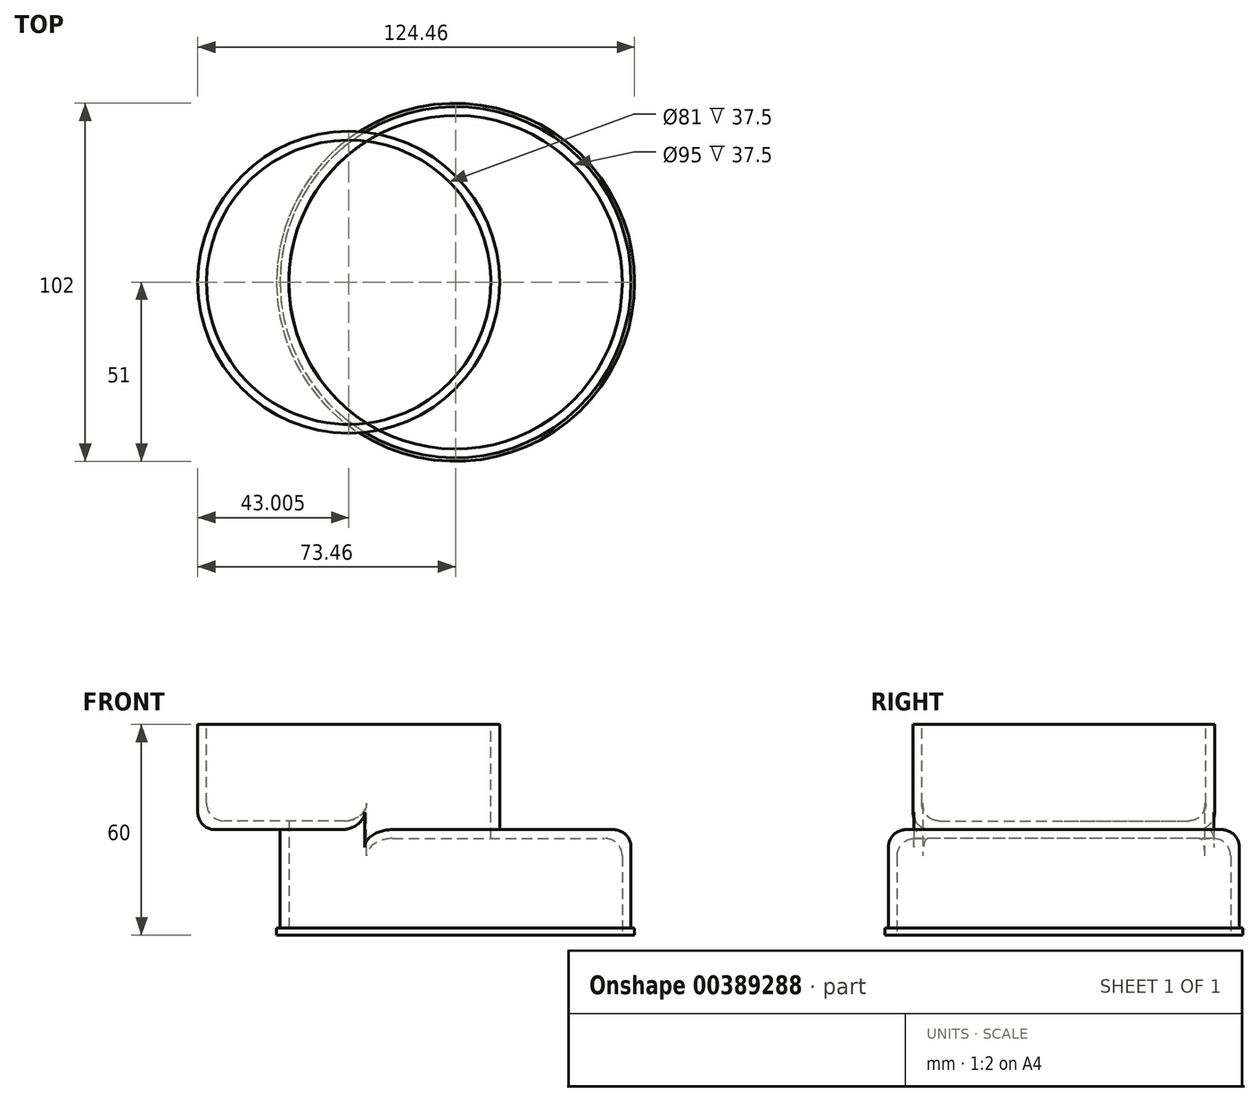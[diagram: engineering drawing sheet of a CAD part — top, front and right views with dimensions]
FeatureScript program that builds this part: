
annotation { "Feature Type Name" : "Feature", "Feature Type Description" : "" }
export const myFeature = defineFeature(function(context is Context, id is Id, definition is map)
    precondition{}
    {
        {
            var Q0;
            Q0=qCreatedBy(makeId("Front.planeOp"),FACE);
            var sketch = newSketch(context, id + "F0", { "sketchPlane" : qUnion([Q0])});
            skLineSegment(sketch, "E0.bottom", {"start": v(0, 0) * mm, "end": v(-50, 0) * mm});
            skLineSegment(sketch, "E0.top", {"start": v(0, 30) * mm, "end": v(-50, 30) * mm});
            skLineSegment(sketch, "E0.left", {"start": v(0, 0) * mm, "end": v(0, 30) * mm});
            skLineSegment(sketch, "E0.right", {"start": v(-50, 0) * mm, "end": v(-50, 30) * mm});
            skLineSegment(sketch, "E1.bottom", {"start": v(-50, 0) * mm, "end": v(-51, 0) * mm});
            skLineSegment(sketch, "E1.top", {"start": v(-50, 2) * mm, "end": v(-51, 2) * mm});
            skLineSegment(sketch, "E1.left", {"start": v(-50, 0) * mm, "end": v(-50, 2) * mm});
            skLineSegment(sketch, "E1.right", {"start": v(-51, 0) * mm, "end": v(-51, 2) * mm});
            skSolve(sketch);
        }
        {
            var Q0;
            Q0=makeQuery(id+"F0.imprint","IMPRINT",FACE,{"disambiguationData":[TD([[makeQuery(id+"F0.imprint","IMPRINT",EDGE,{"derivedFrom":sQuery(id+"F0.wireOp",EDGE,"E0.bottom")}),-1.0]])]});
            var Q1;
            {var subQ0=sQuery(id+"F0.wireOp",EDGE,"E1.bottom");Q1=makeQuery(id+"F0.imprint","IMPRINT",FACE,{"disambiguationData":[TD([[makeQuery(id+"F0.imprint","IMPRINT",EDGE,{"derivedFrom":subQ0}),-1.0]])]});}
            var Q2;
            Q2=sQuery(id+"F0.wireOp",EDGE,"E0.left");
            revolve(context, id + "F1", {"surfaceOperationType" : NewSurfaceOperationType.NEW, "entities" : qUnion([Q0, Q1]), "axis" : qUnion([Q2]), "revolveType" : RevolveType.FULL});
        }
        {
            var Q0;
            Q0=qCreatedBy(makeId("Front.planeOp"),FACE);
            var sketch = newSketch(context, id + "F2", { "sketchPlane" : qUnion([Q0])});
            skLineSegment(sketch, "E2.bottom", {"start": v(-73.46, 60) * mm, "end": v(-30.46, 60) * mm});
            skLineSegment(sketch, "E2.top", {"start": v(-73.46, 30) * mm, "end": v(-30.46, 30) * mm});
            skLineSegment(sketch, "E2.left", {"start": v(-73.46, 60) * mm, "end": v(-73.46, 30) * mm});
            skLineSegment(sketch, "E2.right", {"start": v(-30.46, 60) * mm, "end": v(-30.46, 30) * mm});
            skSolve(sketch);
        }
        {
            var Q0;
            Q0=makeQuery(id+"F2.imprint","IMPRINT",FACE,{"disambiguationData":[TD([[makeQuery(id+"F2.imprint","IMPRINT",EDGE,{"derivedFrom":sQuery(id+"F2.wireOp",EDGE,"E2.bottom")}),-1.0]])]});
            var Q1;
            Q1=qConstructionFilter(qBodyType(qCreatedBy(id+"F2",EDGE),BodyType.WIRE),ConstructionObject.NO);
            var Q2;
            Q2=sQuery(id+"F2.wireOp",EDGE,"E2.right");
            revolve(context, id + "F3", {"surfaceOperationType" : NewSurfaceOperationType.NEW, "entities" : qUnion([Q0]), "surfaceEntities" : qUnion([Q1]), "axis" : qUnion([Q2]), "revolveType" : RevolveType.FULL});
        }
        {
            var Q0;
            Q0=makeQuery(id+"F3.opRevolve","SWEPT_BODY",BODY,{"disambiguationData":[OSD([sQuery(id+"F2.wireOp",EDGE,"E2.bottom"),sQuery(id+"F2.wireOp",EDGE,"E2.top"),sQuery(id+"F2.wireOp",EDGE,"E2.left"),sQuery(id+"F2.wireOp",EDGE,"E2.right")])]});
            var Q1;
            Q1=makeQuery(id+"F1.opRevolve","SWEPT_BODY",BODY,{"disambiguationData":[OSD([sQuery(id+"F0.wireOp",EDGE,"E0.bottom"),sQuery(id+"F0.wireOp",EDGE,"E0.top"),sQuery(id+"F0.wireOp",EDGE,"E0.left"),sQuery(id+"F0.wireOp",EDGE,"E0.right")])]});
            booleanBodies(context, id + "F4", {"operationType" : BooleanOperationType.UNION, "tools" : qUnion([Q0, Q1])});
        }
        {
            var Q0;
            Q0=makeQuery(id+"F1.opRevolve","SWEPT_FACE",FACE,{"disambiguationData":[OSD([sQuery(id+"F0.wireOp",EDGE,"E0.bottom")])]});
            var Q1;
            Q1=makeQuery(id+"F3.opRevolve","SWEPT_FACE",FACE,{"disambiguationData":[OSD([sQuery(id+"F2.wireOp",EDGE,"E2.bottom")])]});
            shell(context, id + "F5", {"entities" : qUnion([Q0, Q1]), "thickness" : 2.5 * mm});
        }
        {
            var Q0;
            {var subQ0=sQuery(id+"F2.wireOp",EDGE,"E2.left");Q0=makeQuery(id+"F4.opBoolean","SPLIT",EDGE,{"disambiguationData":[topologyDisambiguationEdgeConnected([makeQuery(id+"F1.opRevolve","SWEPT_FACE",FACE,{"disambiguationData":[OSD([sQuery(id+"F0.wireOp",EDGE,"E0.top")])]})])],"derivedFrom":makeQuery(id+"F3.opRevolve","SWEPT_EDGE",EDGE,{"disambiguationData":[OSD([sQuery(id+"F2.wireOp",EDGE,"E2.top"),subQ0])]})});}
            fillet(context, id + "F6", {"entities" : qUnion([Q0]), "tangentPropagation" : true, "radius" : 5 * mm, "defaultsChanged" : false, "vertexSettings" : [], "allowEdgeOverflow" : false});
        }
        {
            var Q0;
            {var subQ0=sQuery(id+"F0.wireOp",EDGE,"E0.right");Q0=makeQuery(id+"F4.opBoolean","SPLIT",EDGE,{"disambiguationData":[topologyDisambiguationEdgeConnected([makeQuery(id+"F3.opRevolve","SWEPT_FACE",FACE,{"disambiguationData":[OSD([sQuery(id+"F2.wireOp",EDGE,"E2.top")])]})])],"derivedFrom":makeQuery(id+"F1.opRevolve","SWEPT_EDGE",EDGE,{"disambiguationData":[OSD([sQuery(id+"F0.wireOp",EDGE,"E0.top"),subQ0])]})});}
            fillet(context, id + "F7", {"entities" : qUnion([Q0]), "tangentPropagation" : true, "radius" : 5 * mm, "defaultsChanged" : false, "vertexSettings" : [], "allowEdgeOverflow" : false});
        }
        {
            var Q0;
            {var subQ0=sQuery(id+"F0.wireOp",EDGE,"E0.right");var subQ1=sQuery(id+"F0.wireOp",EDGE,"E0.top");Q0=makeQuery(id+"F5.opShell","OFFSET_EDGE",EDGE,{"disambiguationData":[OSD([subQ1,subQ0]),TDD([makeQuery(id+"F4.opBoolean","SPLIT",EDGE,{"disambiguationData":[topologyDisambiguationEdgeConnected([makeQuery(id+"F3.opRevolve","SWEPT_FACE",FACE,{"disambiguationData":[OSD([sQuery(id+"F2.wireOp",EDGE,"E2.top")])]})])],"derivedFrom":makeQuery(id+"F1.opRevolve","SWEPT_EDGE",EDGE,{"disambiguationData":[OSD([subQ1,subQ0])]})})])]});}
            fillet(context, id + "F8", {"entities" : qUnion([Q0]), "tangentPropagation" : true, "radius" : 5 * mm, "defaultsChanged" : false, "vertexSettings" : [], "allowEdgeOverflow" : false});
        }
        {
            var Q0;
            {var subQ0=sQuery(id+"F2.wireOp",EDGE,"E2.left");var subQ1=sQuery(id+"F2.wireOp",EDGE,"E2.top");Q0=makeQuery(id+"F5.opShell","OFFSET_EDGE",EDGE,{"disambiguationData":[OSD([subQ1,subQ0]),TDD([makeQuery(id+"F4.opBoolean","SPLIT",EDGE,{"disambiguationData":[topologyDisambiguationEdgeConnected([makeQuery(id+"F1.opRevolve","SWEPT_FACE",FACE,{"disambiguationData":[OSD([sQuery(id+"F0.wireOp",EDGE,"E0.top")])]})])],"derivedFrom":makeQuery(id+"F3.opRevolve","SWEPT_EDGE",EDGE,{"disambiguationData":[OSD([subQ1,subQ0])]})})])]});}
            fillet(context, id + "F9", {"entities" : qUnion([Q0]), "tangentPropagation" : true, "radius" : 5 * mm, "defaultsChanged" : false, "vertexSettings" : [], "allowEdgeOverflow" : false});
        }
    });
